# Revit family: TY2199
name_source: partatom
category: Sprinklers
revit_build: Autodesk Revit 2016 (Build: 20150220_1215(x64)
units: mm (PartAtom-declared; Revit-internal decimal feet)

## family parameters
Always vertical = Yes
Cut with Voids When Loaded = No
Maintain Annotation Orientation = No
OmniClass Number = 23.65.70.17.11.24
OmniClass Title = Fire Fighting Sprinkler Heads
Part Type = Normal
Room Calculation Point = No
Round Connector Dimension = Use Diameter
Shared = No
Work Plane-Based = No

## types (1)
- CC3 Combustible Concealed Space Upright Sprinklers 1/2" NPT K=4.2 200°F/93°C Brass TY2199 TFP633_51-311-1-200
    COBie = Yes
    COBie.Component.Description = CC3 Wet Upright  93.3°C K60 DN15 NPT Br
    COBie.Component.Name = Sprinklers:Upright_200
    COBie.Type = Yes
    COBie.Type.AssetType = Fixed
    COBie.Type.Category = Pr_70_55_97_84:Sprinklers
    COBie.Type.Colour = Yellow
    COBie.Type.DurationUnit = year
    COBie.Type.Finish = Natural Brass
    COBie.Type.Manufacturer = Tyco Fire Protection Products
    COBie.Type.Material = Brass
    COBie.Type.ModelNumber = 51-311-1-200
    COBie.Type.ModelReference = CC3 Wet Upright  93.3°C K60 DN15 NPT Br
    COBie.Type.NominalHeight = 0 mm  [stored 0 ft]
    COBie.Type.NominalLength = 0 mm  [stored 0 ft]
    COBie.Type.NominalWidth = 0 mm  [stored 0 ft]
    COBie.Type.ReplacementCost = 0 $
    COBie.Type.Shape = Cylinder
    COBie.Type.Size = 1/2"(DN15)
    COBie.Type.WarrantyGuarantorParts = http://tycofsbp.com
TFPPTerms_of_Sale.pdf
    Coverage = Standard
    Description = CC3 Combustible Concealed Space Upright Sprinklers 1/2" NPT K=4.2 200°F/93°C Brass TY2199 TFP633_51-311-1-200
    K-Factor = 59.9322
    Manufacturer = Tyco Fire Protection Products
    Manufacturer URL = www.tyco-fire.com
    Model = CC3
    Nominal Diameter 1 = 15 mm
    Orifice = Standard
    Orifice Size = 0 mm
    Outside Diameter 1 = 21 mm
    Part No = 51-311-1-200
    Response = Quick
    SIN No = TY2199
    Style Id = 0
    Takeout 1 = 57 mm
    Technical Data Sheet No = TFP633
    Temperature Rating = 93 °C

note: [stored X ft] marks values corroborated as IEEE doubles in the binary element streams (Revit-internal decimal feet)

## geometry (parser evidence)
native form markers: Blend x2, Sweep x71
no freeform markers — native parametric forms only
